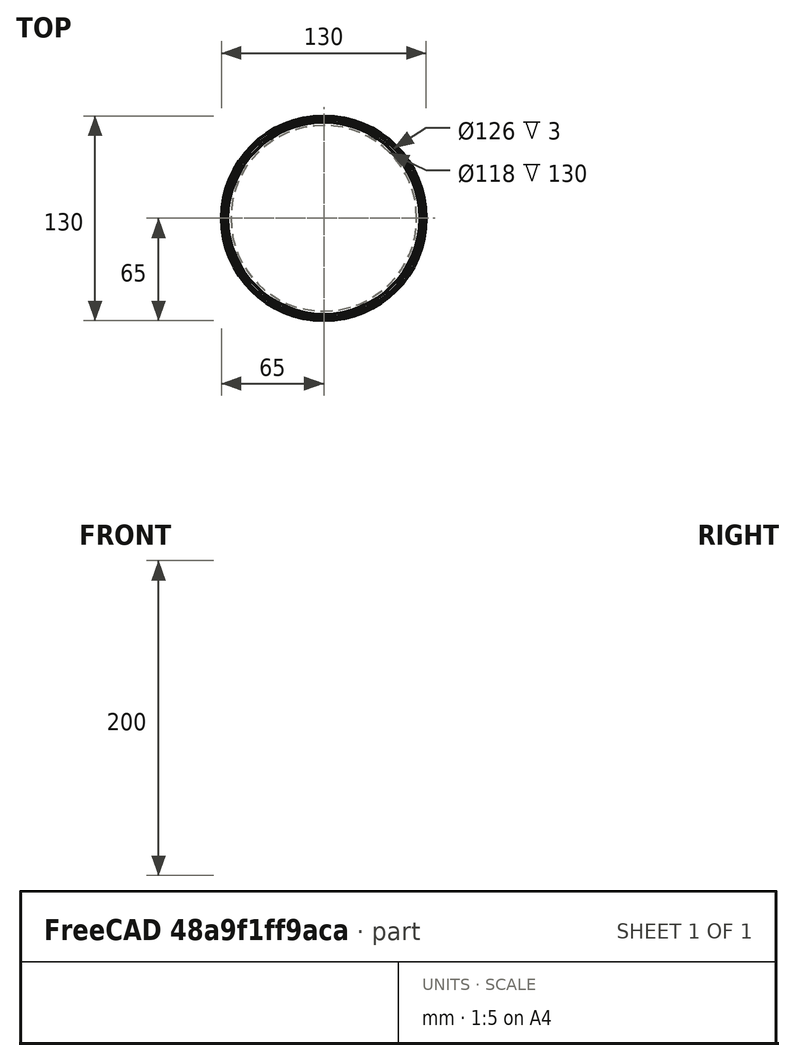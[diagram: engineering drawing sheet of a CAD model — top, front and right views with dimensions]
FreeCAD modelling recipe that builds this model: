
FCSTD DOCUMENT  (FreeCAD 0.22R37730 (Git))
Label: ловушка
License: All rights reserved
LicenseURL: https://en.wikipedia.org/wiki/All_rights_reserved
objects: Sketcher::SketchObject×3, PartDesign::Revolution×1, PartDesign::Body×1, App::Part×1
note: 6 computed .brp shape members not serialized (recipe doc carries the construction recipe); baked Part::Feature solids carry a one-line shape summary decoded from their .brp

FEATURE [Sketcher::SketchObject] Sketch
  AttachmentSupport = -> [XZ_Plane001]
  FullyConstrained = true
  MapMode = 5
  Placement = pos=(0,0,0) rot=(1,0,0;1.5708rad)
  Support = -> [XZ_Plane001]
FEATURE [Sketcher::SketchObject] Sketch001
  AttachmentSupport = -> [XZ_Plane001]
  FullyConstrained = false
  MapMode = 5
  Placement = pos=(0,0,0) rot=(1,0,0;1.5708rad)
  Support = -> [XZ_Plane001]
  sketch-geometry (23):
    g0: LineSegment StartX=65 StartY=0 StartZ=0 EndX=65 EndY=5 EndZ=0
    g1: LineSegment StartX=65 StartY=5 StartZ=0 EndX=63 EndY=5 EndZ=0
    g2: LineSegment StartX=63 StartY=5 StartZ=0 EndX=63 EndY=2 EndZ=0
    g3: LineSegment StartX=63 StartY=2 StartZ=0 EndX=61 EndY=2 EndZ=0
    g4: LineSegment StartX=61 StartY=2 StartZ=0 EndX=61 EndY=132 EndZ=0
    g5: LineSegment StartX=0 StartY=0 StartZ=0 EndX=0 EndY=200 EndZ=0
    g6-g9: Circle x4 (B-spline internal-alignment scaffolding for g10; pole/knot coordinates omitted)
    g10: BSplineCurve PolesCount=4 KnotsCount=2 Degree=3 IsPeriodic=0
    g11: GeomPoint X=0 Y=200 Z=0
    g12: GeomPoint X=61 Y=132 Z=0
    g13: LineSegment StartX=0 StartY=200 StartZ=0 EndX=0 EndY=198 EndZ=0
    g14: LineSegment StartX=65 StartY=0 StartZ=0 EndX=59 EndY=0 EndZ=0
    g15: LineSegment StartX=59 StartY=0 StartZ=0 EndX=59 EndY=130 EndZ=0
    g16-g19: Circle x4 (B-spline internal-alignment scaffolding for g20; pole/knot coordinates omitted)
    g20: BSplineCurve PolesCount=4 KnotsCount=2 Degree=3 IsPeriodic=0
    g21: GeomPoint X=0 Y=198 Z=0
    g22: GeomPoint X=59 Y=130 Z=0
  constraints (48):
    c: PointOnObject(g0,g-1)
    c: Vertical(g0)
    c: Coincident(g1,g0)
    c: Horizontal(g1)
    c: Coincident(g2,g1)
    c: Vertical(g2)
    c: Coincident(g4,g3)
    c: Vertical(g4)
    c: DistanceX(g-1,g0) = 65
    c: Horizontal(g3)
    c: DistanceX(g1,g1) = 2
    c: Coincident(g2,g3)
    c: Distance(g0,g0) = 5
    c: DistanceY(g-1,g3) = 2
    c: DistanceX(g3,g3) = 2
    c: Distance(g4,g4) = 130
    c: Coincident(g5,g-1)
    c: Vertical(g5)
    c: DistanceY(g5,g5) = 200
    c: Weight(g6) = 1
    c: Coincident(g10,g5)
    c: Equal(g6,g7)
    c: Equal(g6,g8)
    c: Coincident(g8,g4)
    c: Equal(g6,g9)
    c: Coincident(g10,g4)
    c: InternalAlignment(g6-g9 -> g10) x4
    c: InternalAlignment(g11,g10)
    c: InternalAlignment(g12,g10)
    c: Coincident(g13,g5)
    c: PointOnObject(g13,g5)
    c: Distance(g13,g13) = 2
    c: Coincident(g14,g0)
    c: PointOnObject(g14,g-1)
    c: DistanceX(g14,g3) = 2
    c: Coincident(g15,g14)
    c: Vertical(g15)
    c: DistanceY(g15,g15) = 130
    c: Weight(g16) = 1
    c: Coincident(g20,g13)
    c: Equal(g16,g17)
    c: Equal(g16,g18)
    c: Coincident(g18,g15)
    c: Equal(g16,g19)
    c: Coincident(g20,g15)
    c: InternalAlignment(g16-g19 -> g20) x4
    c: InternalAlignment(g21,g20)
    c: InternalAlignment(g22,g20)
FEATURE [PartDesign::Revolution] Revolution
  Angle = 360
  Angle2 = 60
  Axis = (0,2e-16,1)
  Base = (0,0,0)
  Placement = pos=(0,0,0) rot=(1,0,0;1.5708rad)
  Profile = -> Sketch001
  ReferenceAxis = -> Sketch001 [V_Axis]
  Reversed = true
  Suppressed = false
  Type = 0
FEATURE [Sketcher::SketchObject] Sketch002
  AttachmentSupport = -> [XY_Plane001]
  FullyConstrained = false
  MapMode = 5
  Support = -> [XY_Plane001]
  sketch-geometry (1):
    g0: Circle CenterX=0 CenterY=0 CenterZ=0 NormalX=0 NormalY=0 NormalZ=1 AngleXU=0 Radius=13.6553
  constraints (1):
    c: Coincident(g0,g-1)
FEATURE [PartDesign::Body] Body  label="Тело"
  AllowCompound = false
  Group = -> [Sketch,Sketch001,Revolution,Sketch002]
  Origin = -> Origin001
  Tip = -> Revolution
FEATURE [App::Part] Part
  Group = -> [Body]
  Origin = -> Origin
